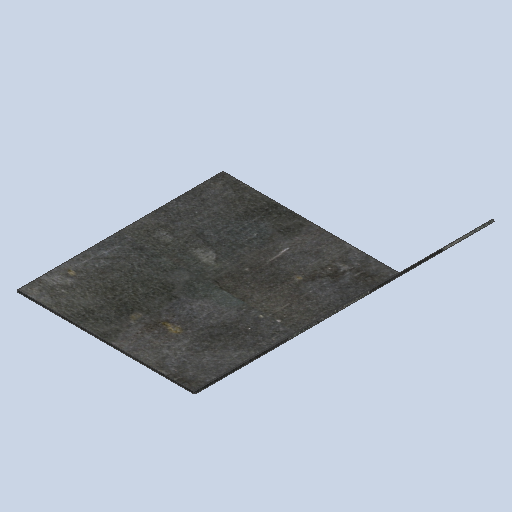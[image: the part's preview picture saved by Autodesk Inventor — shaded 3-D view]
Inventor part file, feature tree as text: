
AUTODESK INVENTOR PART (.ipt)
format: ipt  version: 2024.3 (Build 283343000, 343)  size: 281,088 bytes
history: native  units: mm
features: sheet_metal_op x4, other x4, sketch x3
ambient origin geometry x8: Origin, YZ Plane, XZ Plane, XY Plane, X Axis, Y Axis, Z Axis, Center Point
bodies: Solid1 (feature_tree)
feature tree (11):
  sheet_metal_op  "Face1"
  sheet_metal_op  "Flange1"
  sketch  "Sketch1"  dims[d0=197.0mm]
  other  "Plate1"
  sketch  "Sketch2"  dims[d1=169.946mm]
  other  "Plate2"
  sheet_metal_op  "Bend1"
  sheet_metal_op  "Corner1"
  sketch  "Sketch3"  dims[d2=2.0mm d3=2.0mm d4=1.0mm d5=4.0mm d6=2.0mm d7=127.842mm d8=45.0deg d9=2.0mm d10=8.0mm d11=2.0mm d12=2.0mm d13=100.0mm d14=100.0mm d15=48.5mm d16=2.0mm d17=0.0mm]
  other  "Cut1"
  other  "Definition1"
